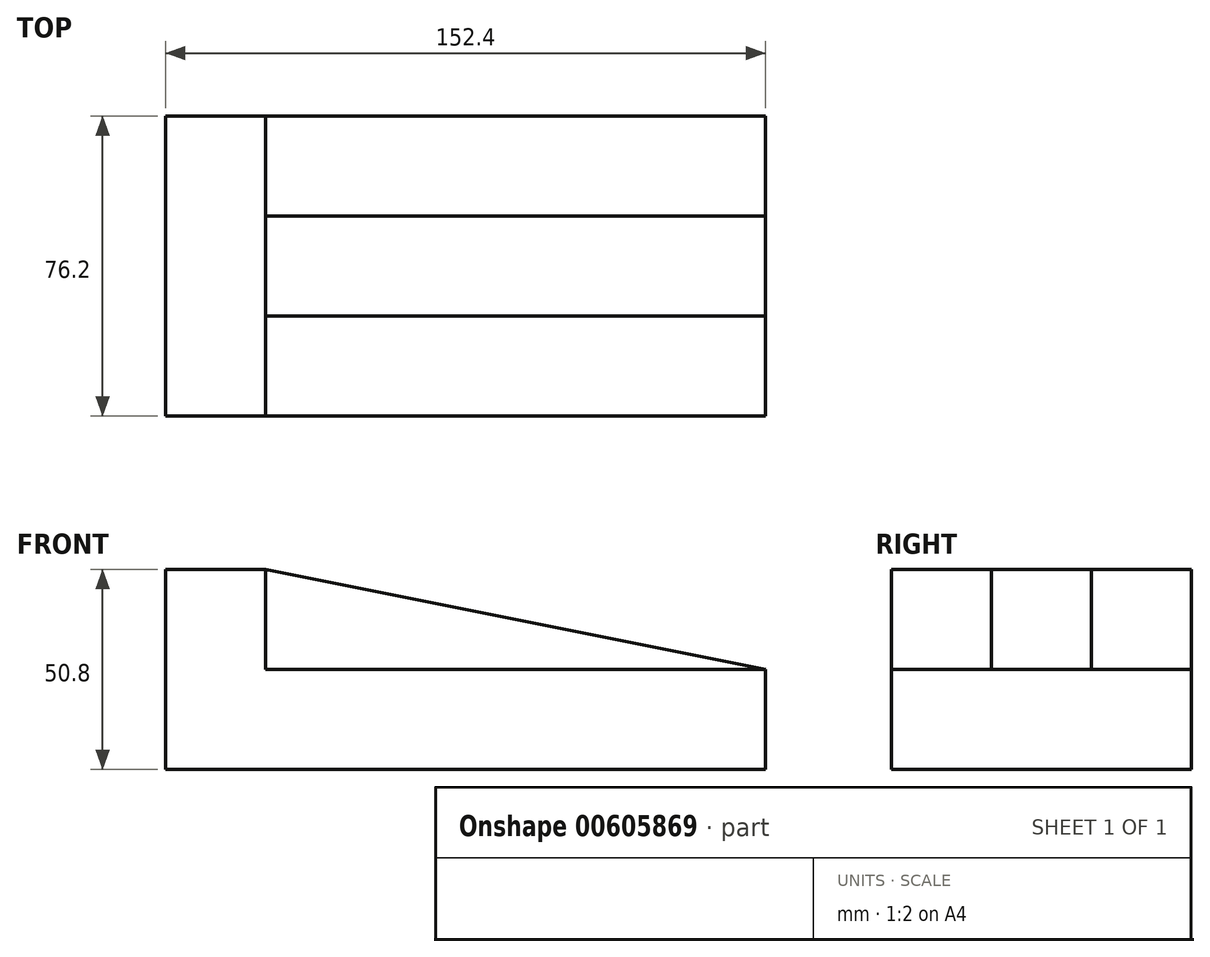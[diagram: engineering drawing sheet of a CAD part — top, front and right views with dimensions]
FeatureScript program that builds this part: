
annotation { "Feature Type Name" : "Feature", "Feature Type Description" : "" }
export const myFeature = defineFeature(function(context is Context, id is Id, definition is map)
    precondition{}
    {
        {
            var Q0;
            Q0=qCreatedBy(makeId("Front.planeOp"),FACE);
            var sketch = newSketch(context, id + "F0", { "sketchPlane" : qUnion([Q0])});
            skLineSegment(sketch, "E0", {"start": v(0, 0) * mm, "end": v(0, 50.8) * mm});
            skLineSegment(sketch, "E1", {"start": v(0, 50.8) * mm, "end": v(25.4, 50.8) * mm});
            skLineSegment(sketch, "E2", {"start": v(25.4, 50.8) * mm, "end": v(25.4, 25.4) * mm});
            skLineSegment(sketch, "E3", {"start": v(25.4, 25.4) * mm, "end": v(152.4, 25.4) * mm});
            skLineSegment(sketch, "E4", {"start": v(152.4, 0) * mm, "end": v(0, 0) * mm});
            skLineSegment(sketch, "E5", {"start": v(152.4, 25.4) * mm, "end": v(152.4, 0) * mm});
            skLineSegment(sketch, "E6", {"start": v(25.4, 50.8) * mm, "end": v(152.4, 25.4) * mm});
            skSolve(sketch);
        }
        {
            var Q0;
            Q0=makeQuery(id+"F0.imprint","IMPRINT",FACE,{"disambiguationData":[TD([[makeQuery(id+"F0.imprint","IMPRINT",EDGE,{"derivedFrom":sQuery(id+"F0.wireOp",EDGE,"E0")}),-1.0]])]});
            var Q1;
            Q1=makeQuery(id+"F0.imprint","IMPRINT",FACE,{"disambiguationData":[TD([[makeQuery(id+"F0.imprint","IMPRINT",EDGE,{"derivedFrom":sQuery(id+"F0.wireOp",EDGE,"E2")}),1.0]])]});
            extrude(context, id + "F1", {"entities" : qUnion([Q0, Q1]), "oppositeDirection" : true, "depth" : 76.2 * mm, "offsetDistance" : 25.4 * mm});
        }
        {
            var Q0;
            Q0=makeQuery(id+"F1.opExtrude","CAP_FACE",FACE,{"disambiguationData":[OSD([sQuery(id+"F0.wireOp",EDGE,"E0"),sQuery(id+"F0.wireOp",EDGE,"E1"),sQuery(id+"F0.wireOp",EDGE,"E4"),sQuery(id+"F0.wireOp",EDGE,"E5"),sQuery(id+"F0.wireOp",EDGE,"E6")])],"isStart":true});
            var sketch = newSketch(context, id + "F2", { "sketchPlane" : qUnion([Q0])});
            skLineSegment(sketch, "E7", {"start": v(25.4, 50.8) * mm, "end": v(25.4, 25.4) * mm});
            skLineSegment(sketch, "E8", {"start": v(25.4, 25.4) * mm, "end": v(152.4, 25.4) * mm});
            skSolve(sketch);
        }
        {
            var Q0;
            Q0=makeQuery(id+"F2.imprint","IMPRINT",FACE,{"disambiguationData":[TD([[makeQuery(id+"F2.imprint","IMPRINT",EDGE,{"derivedFrom":sQuery(id+"F2.wireOp",EDGE,"E7")}),1.0]])]});
            extrude(context, id + "F3", {"entities" : qUnion([Q0]), "operationType" : NewBodyOperationType.REMOVE, "oppositeDirection" : true, "depth" : 25.4 * mm, "offsetDistance" : 25.4 * mm});
        }
        {
            var Q0;
            Q0=makeQuery(id+"F1.opExtrude","CAP_FACE",FACE,{"disambiguationData":[OSD([sQuery(id+"F0.wireOp",EDGE,"E0"),sQuery(id+"F0.wireOp",EDGE,"E1"),sQuery(id+"F0.wireOp",EDGE,"E4"),sQuery(id+"F0.wireOp",EDGE,"E5"),sQuery(id+"F0.wireOp",EDGE,"E6")])],"isStart":false});
            var sketch = newSketch(context, id + "F4", { "sketchPlane" : qUnion([Q0])});
            skLineSegment(sketch, "E9", {"start": v(-25.4, 50.8) * mm, "end": v(-25.4, 25.4) * mm});
            skLineSegment(sketch, "E10", {"start": v(-25.4, 25.4) * mm, "end": v(-152.4, 25.4) * mm});
            skSolve(sketch);
        }
        {
            var Q0;
            Q0=makeQuery(id+"F4.imprint","IMPRINT",FACE,{"disambiguationData":[TD([[makeQuery(id+"F4.imprint","IMPRINT",EDGE,{"derivedFrom":sQuery(id+"F4.wireOp",EDGE,"E9")}),-1.0]])]});
            extrude(context, id + "F5", {"entities" : qUnion([Q0]), "operationType" : NewBodyOperationType.REMOVE, "oppositeDirection" : true, "depth" : 25.4 * mm, "offsetDistance" : 25.4 * mm});
        }
    });
